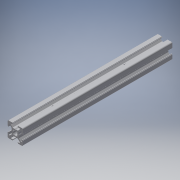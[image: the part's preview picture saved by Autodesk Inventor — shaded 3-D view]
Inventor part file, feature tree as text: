
AUTODESK INVENTOR PART (.ipt)
format: ipt  version: 2016 (Build 200138000, 138)  size: 403,456 bytes
history: native  units: in
note: dims shown in document units (in); Inventor stores cm internally (conversion verified against a paired STEP export)
features: other x3, sketch x2, extrude x1, hole x1, mirror x1
ambient origin geometry x8: Origin, YZ Plane, XZ Plane, XY Plane, X Axis, Y Axis, Z Axis, Center Point
bodies: Solid1 (feature_tree)
feature tree (8):
  other  "Blocks"
  extrude  "Extrusion1"  Depth=2.0in
  hole  "Hole1"  [1 undecoded]
  mirror  "Mirror1"
  sketch  "Sketch1"  dims[d1=0.0in d5=2.0in]
  other  "20x20"
  sketch  "Sketch3"  dims[d6=0.187in d7=0.75in d8=0.375in d9=0.25in d10=0.5635in d11=1.0in d12=0.8108in d13=1.0in d14=1.0in]
  other  "20x20:1"
note: 1 required parameter value undecoded (feature->parameter linkage not recoverable at this tier; creation-order binding heuristic only, values carry confidence <= 0.55)
